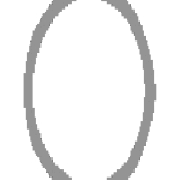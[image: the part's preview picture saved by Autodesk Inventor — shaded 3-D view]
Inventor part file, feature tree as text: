
AUTODESK INVENTOR PART (.ipt)
format: ipt  version: 2021 (Build 250183000, 183)  size: 112,640 bytes
history: native  units: in
note: dims shown in document units (in); Inventor stores cm internally (conversion verified against a paired STEP export)
features: other x4, sketch x3, plane x1
ambient origin geometry x8: Origin, YZ Plane, XZ Plane, XY Plane, X Axis, Y Axis, Z Axis, Center Point
bodies: Solid1 (feature_tree), Body (feature_tree)
feature tree (8):
  other  "Driven Length"
  other  "Frame Generator"
  other  "Start Plane"
  other  "End Plane"
  sketch  "Sketch"  dims[d2=14.4375in d4=-0.0in d5=14.4375in d6=0.12in d7=0.0in d8=90.0deg d9=14.4375in]
  sketch  "Sketch2"  dims[d0=1.0in]
  plane  "Work Plane3"
  sketch  "Sketch3"  dims[d1=0.065in]
